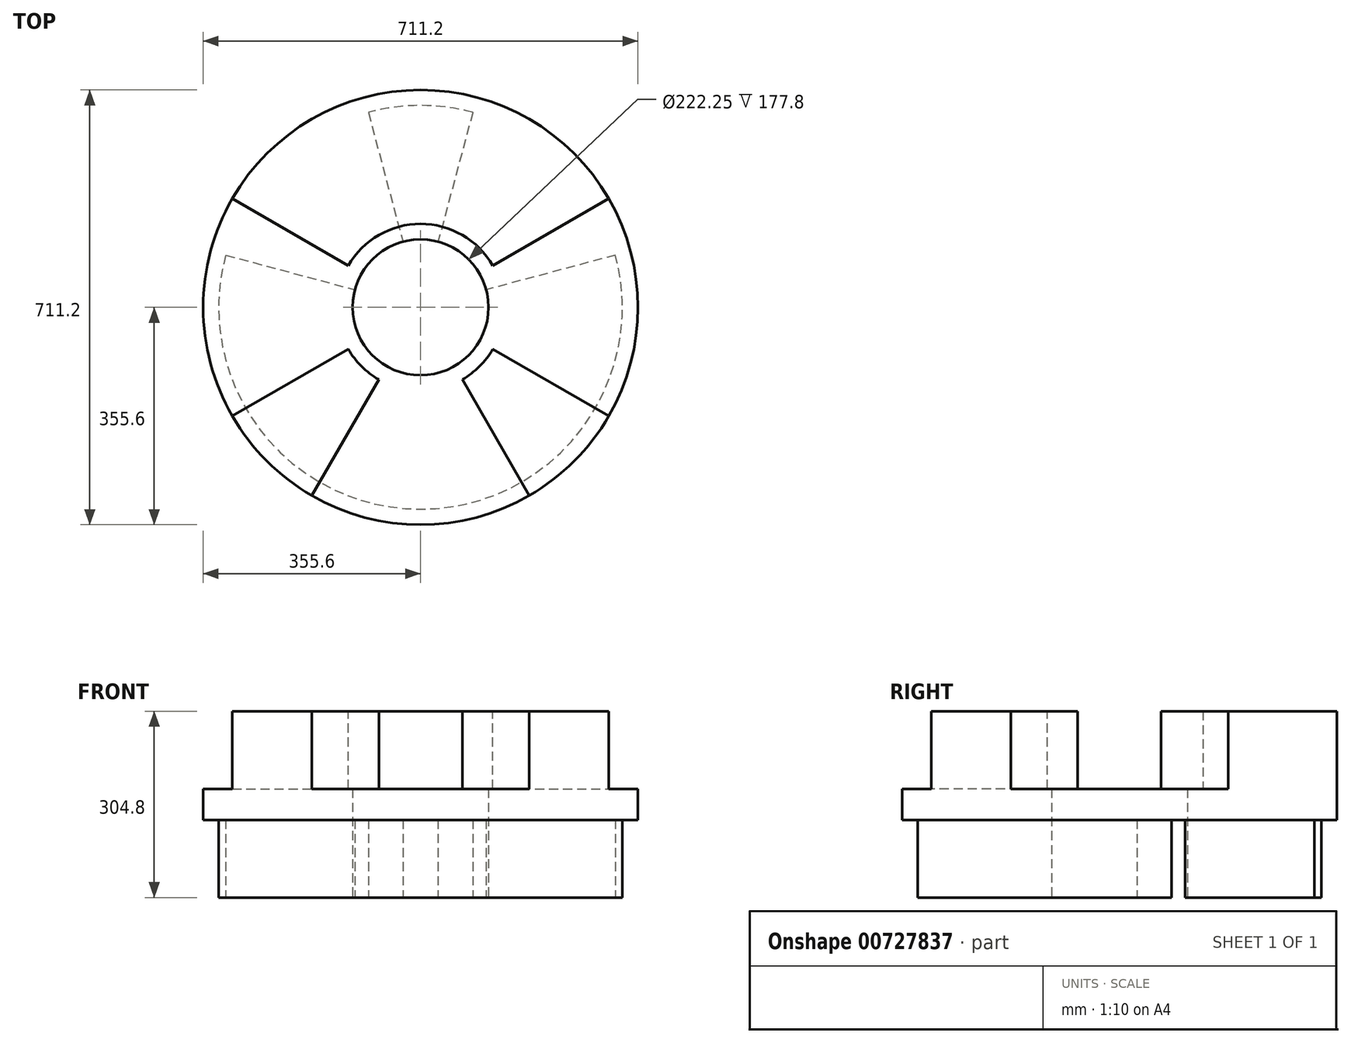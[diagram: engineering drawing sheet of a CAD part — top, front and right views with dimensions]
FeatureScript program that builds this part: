
annotation { "Feature Type Name" : "Feature", "Feature Type Description" : "" }
export const myFeature = defineFeature(function(context is Context, id is Id, definition is map)
    precondition{}
    {
        {
            var Q0;
            Q0=qCreatedBy(makeId("Front.planeOp"),FACE);
            var sketch = newSketch(context, id + "F0", { "sketchPlane" : qUnion([Q0])});
            skLineSegment(sketch, "E0", {"start": v(0, 0) * mm, "end": v(0, 719.83) * mm, "construction": true});
            skLineSegment(sketch, "E1", {"start": v(381, 727.2) * mm, "end": v(381, -112.59) * mm, "construction": true});
            skLineSegment(sketch, "E2", {"start": v(-124.84, 645.16) * mm, "end": v(765.44, 645.16) * mm});
            skLineSegment(sketch, "E3", {"start": v(114.3, -53.81) * mm, "end": v(114.3, 714.98) * mm, "construction": true});
            skLineSegment(sketch, "E4", {"start": v(120.65, 406.95) * mm, "end": v(120.65, 550.02) * mm, "construction": true});
            skLineSegment(sketch, "E5", {"start": v(111.12, 177.8) * mm, "end": v(111.13, 0) * mm});
            skLineSegment(sketch, "E6", {"start": v(-153.27, 177.8) * mm, "end": v(640.71, 177.8) * mm, "construction": true});
            skLineSegment(sketch, "E7", {"start": v(111.13, 0) * mm, "end": v(330.2, 0) * mm});
            skLineSegment(sketch, "E8", {"start": v(111.12, 177.8) * mm, "end": v(136.53, 177.8) * mm});
            skLineSegment(sketch, "E9", {"start": v(136.53, 177.8) * mm, "end": v(136.53, 304.8) * mm});
            skLineSegment(sketch, "E10", {"start": v(136.53, 304.8) * mm, "end": v(355.6, 304.8) * mm});
            skLineSegment(sketch, "E11", {"start": v(355.6, 304.8) * mm, "end": v(355.6, 127) * mm});
            skLineSegment(sketch, "E12", {"start": v(355.6, 127) * mm, "end": v(330.2, 127) * mm});
            skLineSegment(sketch, "E13", {"start": v(330.2, 127) * mm, "end": v(330.2, 0) * mm});
            skSolve(sketch);
        }
        {
            var Q0;
            Q0=makeQuery(id+"F0.imprint","IMPRINT",FACE,{"disambiguationData":[TD([[makeQuery(id+"F0.imprint","IMPRINT",EDGE,{"derivedFrom":sQuery(id+"F0.wireOp",EDGE,"E5")}),1.0]])]});
            var Q1;
            Q1=sQuery(id+"F0.wireOp",EDGE,"E0");
            revolve(context, id + "F1", {"surfaceOperationType" : NewSurfaceOperationType.NEW, "entities" : qUnion([Q0]), "axis" : qUnion([Q1]), "revolveType" : RevolveType.FULL});
        }
        {
            var Q0;
            Q0=makeQuery(id+"F1.opRevolve","SWEPT_FACE",FACE,{"disambiguationData":[OSD([sQuery(id+"F0.wireOp",EDGE,"E10")])]});
            var sketch = newSketch(context, id + "F2", { "sketchPlane" : qUnion([Q0])});
            skLineSegment(sketch, "E14", {"start": v(0, 0) * mm, "end": v(396.92, 0) * mm, "construction": true});
            skLineSegment(sketch, "E15", {"start": v(-329.96, -190.5) * mm, "end": v(329.96, 190.5) * mm});
            skLineSegment(sketch, "E16", {"start": v(-329.96, 190.5) * mm, "end": v(329.96, -190.5) * mm});
            skLineSegment(sketch, "E17", {"start": v(0, 0) * mm, "end": v(190.5, 329.96) * mm});
            skLineSegment(sketch, "E18", {"start": v(190.5, 329.96) * mm, "end": v(-190.5, -329.96) * mm});
            skLineSegment(sketch, "E19", {"start": v(190.5, -329.96) * mm, "end": v(-190.5, 329.96) * mm});
            skLineSegment(sketch, "E20", {"start": v(0, 0) * mm, "end": v(0, 463.63) * mm, "construction": true});
            skArc(sketch, "E21", {"start": v(190.5, 329.96) * mm, "mid": v(0, 381) * mm, "end": v(-190.5, 329.96) * mm});
            skArc(sketch, "E22.trimOffspring", {"start": v(-329.96, 190.5) * mm, "mid": v(-381, 0) * mm, "end": v(-329.96, -190.5) * mm});
            skArc(sketch, "E23.trimOffspring", {"start": v(-190.5, -329.96) * mm, "mid": v(0, -381) * mm, "end": v(190.5, -329.96) * mm});
            skArc(sketch, "E24.trimOffspring", {"start": v(329.96, -190.5) * mm, "mid": v(381, 0) * mm, "end": v(329.96, 190.5) * mm});
            skSolve(sketch);
        }
        {
            var Q0;
            {var subQ0=sQuery(id+"F2.wireOp",EDGE,"E15");var subQ1=sQuery(id+"F0.wireOp",EDGE,"E10");var subQ2=makeQuery(id+"F1.opRevolve","SWEPT_EDGE",EDGE,{"disambiguationData":[OSD([subQ1,sQuery(id+"F0.wireOp",EDGE,"E11")])]});var subQ3=makeQuery(id+"F2.imprint","INTERSECT",VERTEX,{"derivedFrom":[subQ2,subQ0]});Q0=makeQuery(id+"F2.imprint","IMPRINT",FACE,{"disambiguationData":[TD([[makeQuery(id+"F2.imprint","IMPRINT",EDGE,{"disambiguationData":[TD([[subQ3,1.0]])],"derivedFrom":subQ0}),-1.0]])]});}
            var Q1;
            {var subQ0=sQuery(id+"F2.wireOp",EDGE,"E18");var subQ1=sQuery(id+"F0.wireOp",EDGE,"E10");var subQ2=makeQuery(id+"F1.opRevolve","SWEPT_EDGE",EDGE,{"disambiguationData":[OSD([subQ1,sQuery(id+"F0.wireOp",EDGE,"E11")])]});var subQ3=makeQuery(id+"F2.imprint","INTERSECT",VERTEX,{"disambiguationData":[OD(0.0)],"derivedFrom":[subQ2,subQ0]});Q1=makeQuery(id+"F2.imprint","IMPRINT",FACE,{"disambiguationData":[TD([[makeQuery(id+"F2.imprint","IMPRINT",EDGE,{"disambiguationData":[TD([[subQ3,-1.0]])],"derivedFrom":subQ0}),-1.0]])]});}
            var Q2;
            {var subQ0=sQuery(id+"F2.wireOp",EDGE,"E15");var subQ1=sQuery(id+"F0.wireOp",EDGE,"E10");var subQ2=makeQuery(id+"F1.opRevolve","SWEPT_EDGE",EDGE,{"disambiguationData":[OSD([subQ1,sQuery(id+"F0.wireOp",EDGE,"E11")])]});var subQ3=makeQuery(id+"F2.imprint","INTERSECT",VERTEX,{"disambiguationData":[OD(0.0)],"derivedFrom":[subQ2,subQ0]});Q2=makeQuery(id+"F2.imprint","IMPRINT",FACE,{"disambiguationData":[TD([[makeQuery(id+"F2.imprint","IMPRINT",EDGE,{"disambiguationData":[TD([[subQ3,-1.0]])],"derivedFrom":subQ0}),1.0]])]});}
            var Q3;
            {var subQ0=sQuery(id+"F2.wireOp",EDGE,"E18");var subQ1=sQuery(id+"F0.wireOp",EDGE,"E10");var subQ2=makeQuery(id+"F1.opRevolve","SWEPT_EDGE",EDGE,{"disambiguationData":[OSD([subQ1,sQuery(id+"F0.wireOp",EDGE,"E11")])]});var subQ3=makeQuery(id+"F2.imprint","INTERSECT",VERTEX,{"disambiguationData":[OD(1.0)],"derivedFrom":[subQ2,subQ0]});Q3=makeQuery(id+"F2.imprint","IMPRINT",FACE,{"disambiguationData":[TD([[makeQuery(id+"F2.imprint","IMPRINT",EDGE,{"disambiguationData":[TD([[subQ3,1.0]])],"derivedFrom":subQ0}),1.0]])]});}
            extrude(context, id + "F3", {"entities" : qUnion([Q0, Q1, Q2, Q3]), "operationType" : NewBodyOperationType.REMOVE, "oppositeDirection" : true, "depth" : 127 * mm, "offsetDistance" : 25.4 * mm});
        }
        {
            var Q0;
            Q0=makeQuery(id+"F1.opRevolve","SWEPT_FACE",FACE,{"disambiguationData":[OSD([sQuery(id+"F0.wireOp",EDGE,"E7")])]});
            var sketch = newSketch(context, id + "F4", { "sketchPlane" : qUnion([Q0])});
            skLineSegment(sketch, "E25", {"start": v(0, 0) * mm, "end": v(404.65, 0) * mm, "construction": true});
            skLineSegment(sketch, "E26", {"start": v(0, 0) * mm, "end": v(284.74, 284.74) * mm, "construction": true});
            skCircle(sketch, "E27", {"center": v(0, 0) * mm, "radius": 381 * mm});
            skLineSegment(sketch, "E28", {"start": v(-368.02, -98.61) * mm, "end": v(368.02, 98.61) * mm});
            skLineSegment(sketch, "E29", {"start": v(-98.61, -368.02) * mm, "end": v(98.61, 368.02) * mm});
            skLineSegment(sketch, "E30", {"start": v(0, 0) * mm, "end": v(-303.65, 303.65) * mm, "construction": true});
            skLineSegment(sketch, "E31", {"start": v(368.02, -98.61) * mm, "end": v(-368.02, 98.61) * mm});
            skLineSegment(sketch, "E32", {"start": v(98.61, -368.02) * mm, "end": v(-98.61, 368.02) * mm});
            skSolve(sketch);
        }
        {
            var Q0;
            {var subQ0=sQuery(id+"F4.wireOp",EDGE,"E31");var subQ1=sQuery(id+"F0.wireOp",EDGE,"E7");var subQ2=makeQuery(id+"F1.opRevolve","SWEPT_EDGE",EDGE,{"disambiguationData":[OSD([sQuery(id+"F0.wireOp",EDGE,"E5"),subQ1])]});var subQ3=makeQuery(id+"F4.imprint","INTERSECT",VERTEX,{"disambiguationData":[OD(1.0)],"derivedFrom":[subQ2,subQ0]});Q0=makeQuery(id+"F4.imprint","IMPRINT",FACE,{"disambiguationData":[TD([[makeQuery(id+"F4.imprint","IMPRINT",EDGE,{"disambiguationData":[TD([[subQ3,-1.0]])],"derivedFrom":subQ0}),-1.0]])]});}
            var Q1;
            {var subQ0=sQuery(id+"F4.wireOp",EDGE,"E28");var subQ1=sQuery(id+"F0.wireOp",EDGE,"E7");var subQ2=makeQuery(id+"F1.opRevolve","SWEPT_EDGE",EDGE,{"disambiguationData":[OSD([sQuery(id+"F0.wireOp",EDGE,"E5"),subQ1])]});var subQ3=makeQuery(id+"F4.imprint","INTERSECT",VERTEX,{"disambiguationData":[OD(1.0)],"derivedFrom":[subQ2,subQ0]});Q1=makeQuery(id+"F4.imprint","IMPRINT",FACE,{"disambiguationData":[TD([[makeQuery(id+"F4.imprint","IMPRINT",EDGE,{"disambiguationData":[TD([[subQ3,-1.0]])],"derivedFrom":subQ0}),1.0]])]});}
            var Q2;
            {var subQ0=sQuery(id+"F4.wireOp",EDGE,"E31");var subQ1=sQuery(id+"F0.wireOp",EDGE,"E7");var subQ2=makeQuery(id+"F1.opRevolve","SWEPT_EDGE",EDGE,{"disambiguationData":[OSD([subQ1,sQuery(id+"F0.wireOp",EDGE,"E13")])]});var subQ3=makeQuery(id+"F4.imprint","INTERSECT",VERTEX,{"disambiguationData":[OD(0.0)],"derivedFrom":[subQ2,subQ0]});Q2=makeQuery(id+"F4.imprint","IMPRINT",FACE,{"disambiguationData":[TD([[makeQuery(id+"F4.imprint","IMPRINT",EDGE,{"disambiguationData":[TD([[subQ3,-1.0]])],"derivedFrom":subQ0}),1.0]])]});}
            var Q3;
            {var subQ0=sQuery(id+"F4.wireOp",EDGE,"E28");var subQ1=sQuery(id+"F0.wireOp",EDGE,"E7");var subQ2=makeQuery(id+"F1.opRevolve","SWEPT_EDGE",EDGE,{"disambiguationData":[OSD([subQ1,sQuery(id+"F0.wireOp",EDGE,"E13")])]});var subQ3=makeQuery(id+"F4.imprint","INTERSECT",VERTEX,{"disambiguationData":[OD(0.0)],"derivedFrom":[subQ2,subQ0]});Q3=makeQuery(id+"F4.imprint","IMPRINT",FACE,{"disambiguationData":[TD([[makeQuery(id+"F4.imprint","IMPRINT",EDGE,{"disambiguationData":[TD([[subQ3,-1.0]])],"derivedFrom":subQ0}),-1.0]])]});}
            extrude(context, id + "F5", {"entities" : qUnion([Q0, Q1, Q2, Q3]), "operationType" : NewBodyOperationType.REMOVE, "oppositeDirection" : true, "depth" : 127 * mm, "offsetDistance" : 25.4 * mm});
        }
    });
